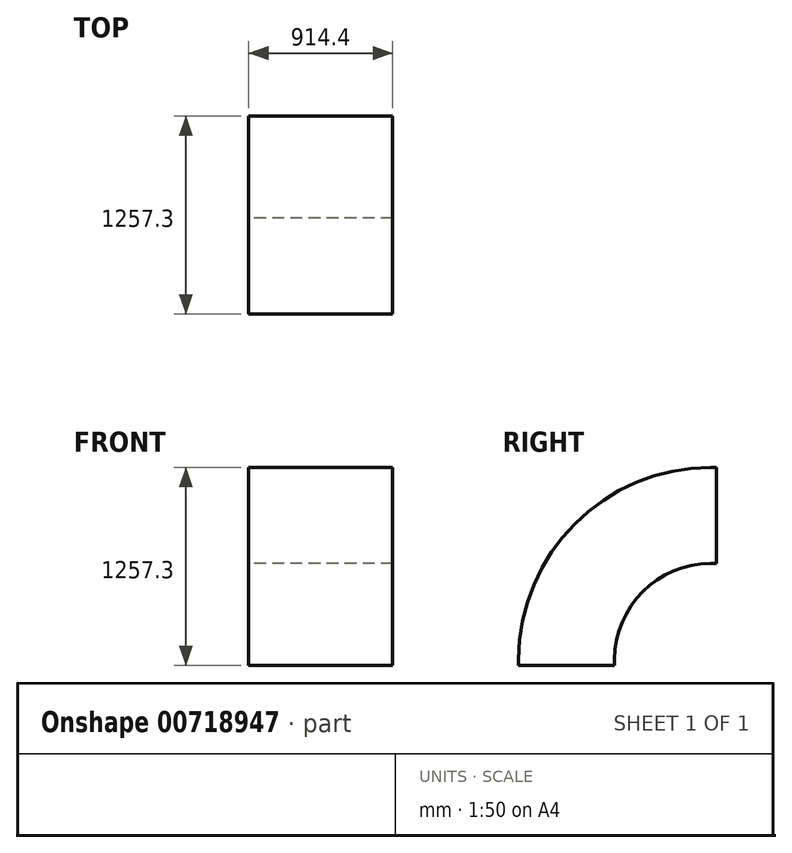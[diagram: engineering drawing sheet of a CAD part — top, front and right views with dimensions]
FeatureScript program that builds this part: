
annotation { "Feature Type Name" : "Feature", "Feature Type Description" : "" }
export const myFeature = defineFeature(function(context is Context, id is Id, definition is map)
    precondition{}
    {
        {
            var Q0;
            Q0=qCreatedBy(makeId("Top.planeOp"),FACE);
            var sketch = newSketch(context, id + "F0", { "sketchPlane" : qUnion([Q0])});
            skLineSegment(sketch, "E0.bottom", {"start": v(457.2, 304.8) * mm, "end": v(-457.2, 304.8) * mm});
            skLineSegment(sketch, "E0.top", {"start": v(457.2, -304.8) * mm, "end": v(-457.2, -304.8) * mm});
            skLineSegment(sketch, "E0.left", {"start": v(457.2, 304.8) * mm, "end": v(457.2, -304.8) * mm});
            skLineSegment(sketch, "E0.right", {"start": v(-457.2, 304.8) * mm, "end": v(-457.2, -304.8) * mm});
            skPoint(sketch, "E0.middle", {"position": v(0, 0) * mm});
            skSolve(sketch);
        }
        {
            var Q0;
            Q0=makeQuery(id+"F0.imprint","IMPRINT",FACE,{"disambiguationData":[TD([[makeQuery(id+"F0.imprint","IMPRINT",EDGE,{"derivedFrom":sQuery(id+"F0.wireOp",EDGE,"E0.bottom")}),1.0]])]});
            extrude(context, id + "F1", {"entities" : qUnion([Q0]), "depth" : 38.1 * mm, "offsetDistance" : 25.4 * mm});
        }
        {
            var Q0;
            Q0=makeQuery(id+"F1.opExtrude","CAP_FACE",FACE,{"disambiguationData":[OSD([sQuery(id+"F0.wireOp",EDGE,"E0.bottom"),sQuery(id+"F0.wireOp",EDGE,"E0.top"),sQuery(id+"F0.wireOp",EDGE,"E0.left"),sQuery(id+"F0.wireOp",EDGE,"E0.right")])],"isStart":false});
            var sketch = newSketch(context, id + "F2", { "sketchPlane" : qUnion([Q0])});
            skLineSegment(sketch, "E1", {"start": v(0, 0) * mm, "end": v(0, 914.4) * mm, "construction": true});
            skPoint(sketch, "E1.endSnap0", {"position": v(0, 304.8) * mm});
            skLineSegment(sketch, "E2", {"start": v(0, 914.4) * mm, "end": v(-206.41, 914.4) * mm});
            skSolve(sketch);
        }
        {
            var Q0;
            Q0=makeQuery(id+"F2.imprint","IMPRINT",FACE,{"disambiguationData":[TD([[makeQuery(id+"F2.imprint","IMPRINT",EDGE,{"derivedFrom":makeQuery(id+"F1.opExtrude","CAP_EDGE",EDGE,{"disambiguationData":[OSD([sQuery(id+"F0.wireOp",EDGE,"E0.bottom")])],"isStart":false})}),1.0]])]});
            var Q1;
            Q1=sQuery(id+"F2.wireOp",EDGE,"E2");
            revolve(context, id + "F3", {"operationType" : NewBodyOperationType.ADD, "surfaceOperationType" : NewSurfaceOperationType.NEW, "entities" : qUnion([Q0]), "axis" : qUnion([Q1]), "revolveType" : RevolveType.ONE_DIRECTION, "angle" : 90 * degree});
        }
        {
            var Q0;
            Q0=makeQuery(id+"F3.opRevolve","CAP_FACE",FACE,{"disambiguationData":[OSD([sQuery(id+"F0.wireOp",EDGE,"E0.bottom"),sQuery(id+"F0.wireOp",EDGE,"E0.top"),sQuery(id+"F0.wireOp",EDGE,"E0.left"),sQuery(id+"F0.wireOp",EDGE,"E0.right")])],"isStart":false});
            extrude(context, id + "F4", {"entities" : qUnion([Q0]), "operationType" : NewBodyOperationType.ADD, "depth" : 38.1 * mm, "offsetDistance" : 25.4 * mm});
        }
    });
